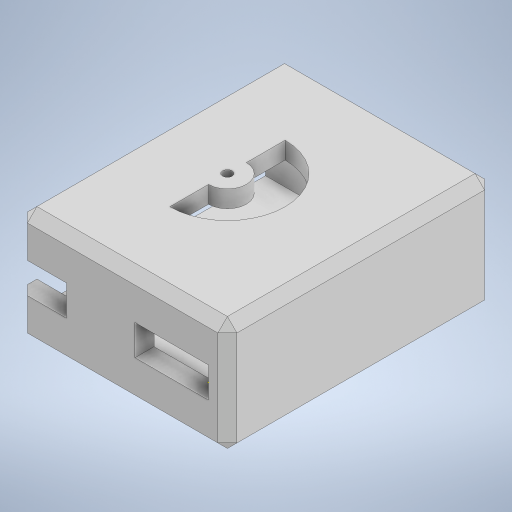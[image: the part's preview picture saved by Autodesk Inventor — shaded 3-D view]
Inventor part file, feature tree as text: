
AUTODESK INVENTOR PART (.ipt)
format: ipt  version: 2023 (Build 270158000, 158)  size: 269,824 bytes
history: native  units: in
note: dims shown in document units (in); Inventor stores cm internally (conversion verified against a paired STEP export)
features: extrude x6, sketch x3, chamfer x1
ambient origin geometry x8: Origin, YZ Plane, XZ Plane, XY Plane, X Axis, Y Axis, Z Axis, Center Point
bodies: Solid1 (feature_tree)
feature tree (10):
  sketch  "Sketch1"  dims[d0=3.0in d1=3.0in]
  extrude  "Extrusion1"  Depth=3.0in
  extrude  "Extrusion2"  Depth=0.25in
  extrude  "Extrusion3"  Depth=0.9in
  extrude  "Extrusion4"  Depth=0.9in
  extrude  "Extrusion5"  Depth=1.5in TaperAngle=0.0deg
  chamfer  "Chamfer1"  Distance=1.05in
  extrude  "Extrusion6"  Depth=0.9in
  sketch  "Sketch3"  dims[d4=0.25in d6=0.5in d7=0.24in d8=1.5in d9=0.0in d10=1.05in d11=0.0in d12=0.125in d13=1.05in d14=0.0in d15=1.05in d16=0.0in d17=3.0in d18=0.0in d19=0.125in d20=0.125in d21=45.0deg d22=0.2in d23=0.4in d24=5.0in d25=0.0in d26=0.9634in d27=0.9in]
  sketch  "Sketch2"  dims[d2=0.25in d3=0.25in]
